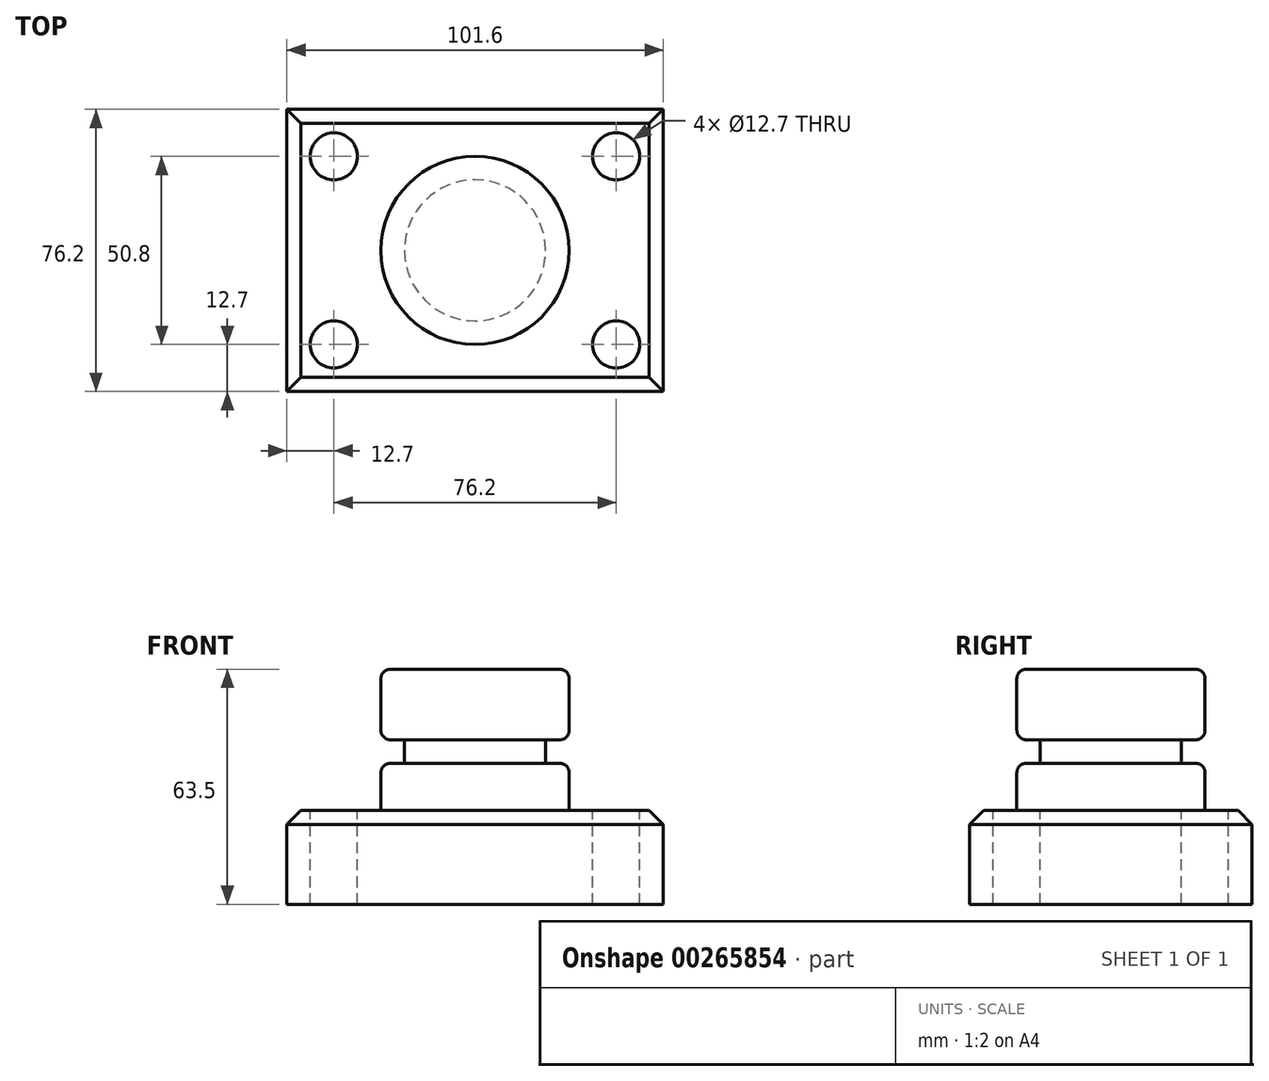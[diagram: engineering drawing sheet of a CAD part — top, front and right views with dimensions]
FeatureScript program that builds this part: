
annotation { "Feature Type Name" : "Feature", "Feature Type Description" : "" }
export const myFeature = defineFeature(function(context is Context, id is Id, definition is map)
    precondition{}
    {
        {
            var Q0;
            Q0=qCreatedBy(makeId("Top.planeOp"),FACE);
            var sketch = newSketch(context, id + "F0", { "sketchPlane" : qUnion([Q0])});
            skLineSegment(sketch, "E0.bottom", {"start": v(0, 0) * mm, "end": v(101.6, 0) * mm});
            skLineSegment(sketch, "E0.top", {"start": v(0, 76.2) * mm, "end": v(101.6, 76.2) * mm});
            skLineSegment(sketch, "E0.left", {"start": v(0, 0) * mm, "end": v(0, 76.2) * mm});
            skLineSegment(sketch, "E0.right", {"start": v(101.6, 0) * mm, "end": v(101.6, 76.2) * mm});
            skSolve(sketch);
        }
        {
            var Q0;
            Q0=makeQuery(id+"F0.imprint","IMPRINT",FACE,{"disambiguationData":[TD([[makeQuery(id+"F0.imprint","IMPRINT",EDGE,{"derivedFrom":sQuery(id+"F0.wireOp",EDGE,"E0.bottom")}),1.0]])]});
            extrude(context, id + "F1", {"entities" : qUnion([Q0]), "depth" : 25.4 * mm});
        }
        {
            var Q0;
            Q0=makeQuery(id+"F1.opExtrude","CAP_FACE",FACE,{"disambiguationData":[OSD([sQuery(id+"F0.wireOp",EDGE,"E0.bottom"),sQuery(id+"F0.wireOp",EDGE,"E0.top"),sQuery(id+"F0.wireOp",EDGE,"E0.left"),sQuery(id+"F0.wireOp",EDGE,"E0.right")])],"isStart":false});
            var sketch = newSketch(context, id + "F2", { "sketchPlane" : qUnion([Q0])});
            skCircle(sketch, "E1", {"center": v(12.7, 63.5) * mm, "radius": 6.35 * mm});
            skCircle(sketch, "E2", {"center": v(88.9, 12.7) * mm, "radius": 6.35 * mm});
            skCircle(sketch, "E3", {"center": v(88.9, 63.5) * mm, "radius": 6.35 * mm});
            skCircle(sketch, "E4", {"center": v(12.7, 12.7) * mm, "radius": 6.35 * mm});
            skSolve(sketch);
        }
        {
            var Q0;
            Q0 = qSketchRegion(id + "F2", true);
            extrude(context, id + "F3", {"entities" : qUnion([Q0]), "operationType" : NewBodyOperationType.REMOVE, "oppositeDirection" : true, "depth" : 25.4 * mm});
        }
        {
            var Q0;
            Q0=makeQuery(id+"F1.opExtrude","CAP_FACE",FACE,{"disambiguationData":[OSD([sQuery(id+"F0.wireOp",EDGE,"E0.bottom"),sQuery(id+"F0.wireOp",EDGE,"E0.top"),sQuery(id+"F0.wireOp",EDGE,"E0.left"),sQuery(id+"F0.wireOp",EDGE,"E0.right")])],"isStart":false});
            var sketch = newSketch(context, id + "F4", { "sketchPlane" : qUnion([Q0])});
            skCircle(sketch, "E5", {"center": v(50.8, 38.1) * mm, "radius": 25.4 * mm});
            skSolve(sketch);
        }
        {
            var Q0;
            Q0 = qSketchRegion(id + "F4", true);
            extrude(context, id + "F5", {"entities" : qUnion([Q0]), "operationType" : NewBodyOperationType.ADD, "depth" : 12.7 * mm});
        }
        {
            var Q0;
            Q0=makeQuery(id+"F5.opExtrude","CAP_FACE",FACE,{"disambiguationData":[OSD([sQuery(id+"F4.wireOp",EDGE,"E5")])],"isStart":false});
            var sketch = newSketch(context, id + "F6", { "sketchPlane" : qUnion([Q0])});
            skCircle(sketch, "E6", {"center": v(50.8, 38.1) * mm, "radius": 19.05 * mm});
            skSolve(sketch);
        }
        {
            var Q0;
            Q0 = qSketchRegion(id + "F6", true);
            extrude(context, id + "F7", {"entities" : qUnion([Q0]), "operationType" : NewBodyOperationType.ADD, "depth" : 6.35 * mm});
        }
        {
            var Q0;
            Q0=makeQuery(id+"F7.opExtrude","CAP_FACE",FACE,{"disambiguationData":[OSD([sQuery(id+"F6.wireOp",EDGE,"E6")])],"isStart":false});
            var sketch = newSketch(context, id + "F8", { "sketchPlane" : qUnion([Q0])});
            skCircle(sketch, "E7", {"center": v(50.8, 38.1) * mm, "radius": 25.4 * mm});
            skSolve(sketch);
        }
        {
            var Q0;
            Q0 = qSketchRegion(id + "F8", true);
            extrude(context, id + "F9", {"entities" : qUnion([Q0]), "operationType" : NewBodyOperationType.ADD, "depth" : 19.05 * mm});
        }
        {
            var Q0;
            Q0=makeQuery(id+"F1.opExtrude","CAP_EDGE",EDGE,{"disambiguationData":[OSD([sQuery(id+"F0.wireOp",EDGE,"E0.right")])],"isStart":false});
            var Q1;
            Q1=makeQuery(id+"F1.opExtrude","CAP_EDGE",EDGE,{"disambiguationData":[OSD([sQuery(id+"F0.wireOp",EDGE,"E0.bottom")])],"isStart":false});
            var Q2;
            Q2=makeQuery(id+"F1.opExtrude","CAP_EDGE",EDGE,{"disambiguationData":[OSD([sQuery(id+"F0.wireOp",EDGE,"E0.top")])],"isStart":false});
            var Q3;
            Q3=makeQuery(id+"F1.opExtrude","CAP_EDGE",EDGE,{"disambiguationData":[OSD([sQuery(id+"F0.wireOp",EDGE,"E0.left")])],"isStart":false});
            chamfer(context, id + "F10", {"entities" : qUnion([Q0, Q1, Q2, Q3]), "width" : 3.8 * mm, "tangentPropagation" : true});
        }
        {
            var Q0;
            Q0=makeQuery(id+"F5.opExtrude","CAP_EDGE",EDGE,{"disambiguationData":[OSD([sQuery(id+"F4.wireOp",EDGE,"E5")])],"isStart":true});
            var Q1;
            Q1=makeQuery(id+"F5.opExtrude","CAP_EDGE",EDGE,{"disambiguationData":[OSD([sQuery(id+"F4.wireOp",EDGE,"E5")])],"isStart":false});
            var Q2;
            Q2=makeQuery(id+"F7.opExtrude","CAP_EDGE",EDGE,{"disambiguationData":[OSD([sQuery(id+"F6.wireOp",EDGE,"E6")])],"isStart":true});
            var Q3;
            Q3=makeQuery(id+"F9.opExtrude","CAP_EDGE",EDGE,{"disambiguationData":[OSD([sQuery(id+"F8.wireOp",EDGE,"E7")])],"isStart":true});
            var Q4;
            Q4=makeQuery(id+"F7.opExtrude","CAP_EDGE",EDGE,{"disambiguationData":[OSD([sQuery(id+"F6.wireOp",EDGE,"E6")])],"isStart":false});
            var Q5;
            Q5=makeQuery(id+"F9.opExtrude","CAP_EDGE",EDGE,{"disambiguationData":[OSD([sQuery(id+"F8.wireOp",EDGE,"E7")])],"isStart":false});
            fillet(context, id + "F11", {"entities" : qUnion([Q0, Q1, Q2, Q3, Q4, Q5]), "radius" : 2.54 * mm, "tangentPropagation" : true, "allowEdgeOverflow" : false});
        }
    });
